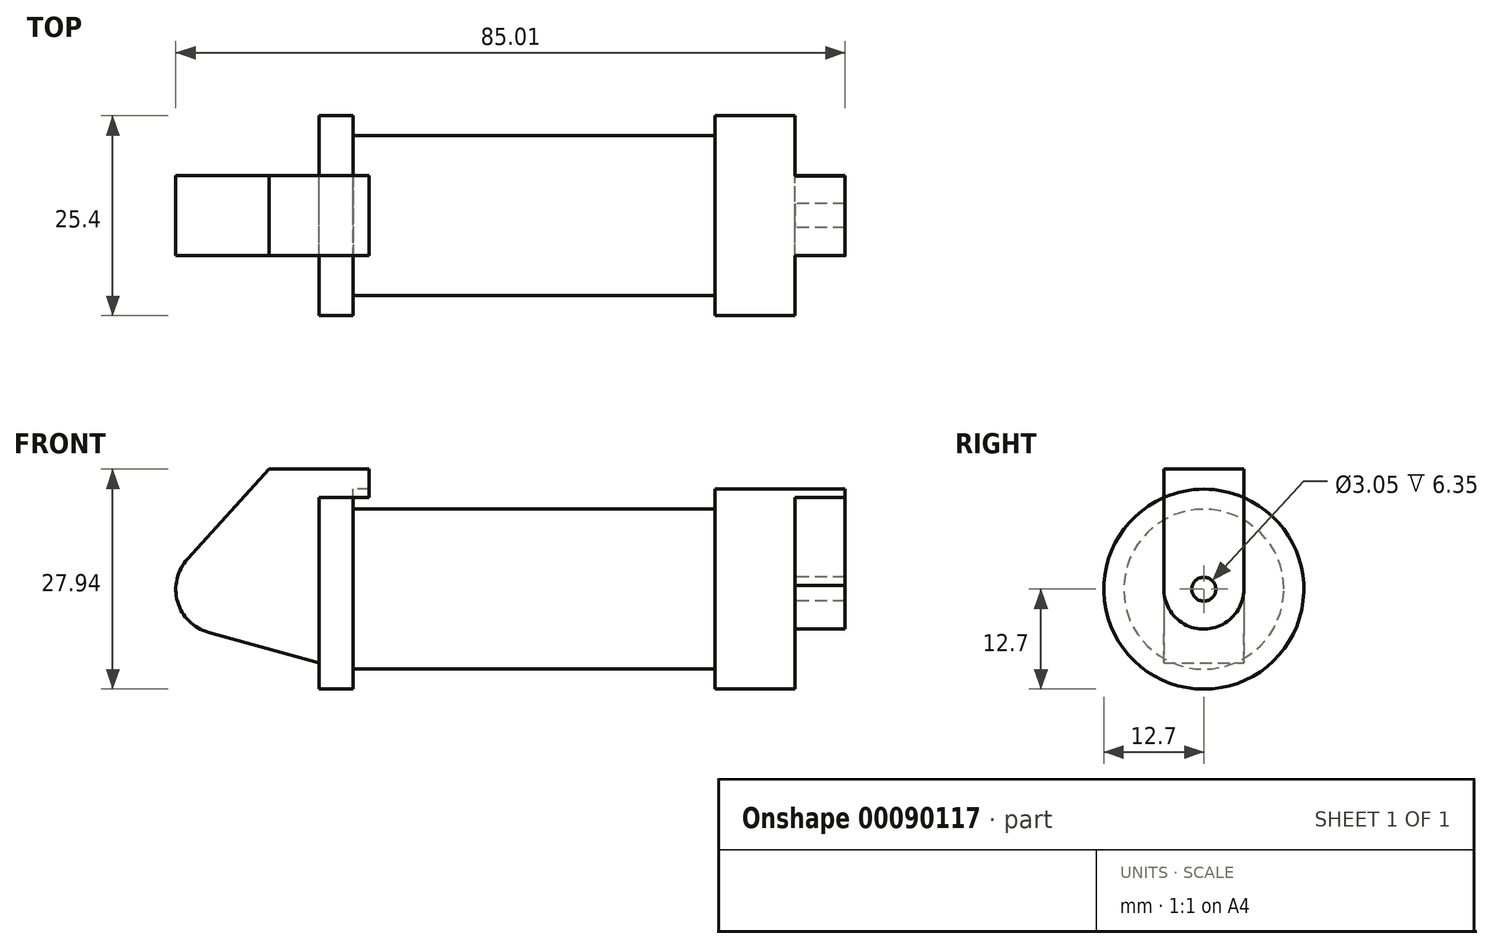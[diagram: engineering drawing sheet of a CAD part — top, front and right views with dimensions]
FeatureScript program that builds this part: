
annotation { "Feature Type Name" : "Feature", "Feature Type Description" : "" }
export const myFeature = defineFeature(function(context is Context, id is Id, definition is map)
    precondition{}
    {
        {
            var Q0;
            Q0=qCreatedBy(makeId("Front.planeOp"),FACE);
            var sketch = newSketch(context, id + "F0", { "sketchPlane" : qUnion([Q0])});
            skLineSegment(sketch, "E0", {"start": v(0, 0) * mm, "end": v(0, 12.7) * mm});
            skLineSegment(sketch, "E1", {"start": v(0, 12.7) * mm, "end": v(10.16, 12.7) * mm});
            skLineSegment(sketch, "E2", {"start": v(10.16, 12.7) * mm, "end": v(10.16, 10.16) * mm});
            skLineSegment(sketch, "E3", {"start": v(10.16, 10.16) * mm, "end": v(56.13, 10.16) * mm});
            skLineSegment(sketch, "E4", {"start": v(56.13, 10.16) * mm, "end": v(56.13, 12.7) * mm});
            skLineSegment(sketch, "E5", {"start": v(56.13, 12.7) * mm, "end": v(66.3, 12.7) * mm});
            skLineSegment(sketch, "E6", {"start": v(66.3, 12.7) * mm, "end": v(66.3, 0) * mm});
            skLineSegment(sketch, "E7", {"start": v(66.3, 0) * mm, "end": v(0, 0) * mm});
            skLineSegment(sketch, "E8", {"start": v(5.84, 15.24) * mm, "end": v(-0.5, 15.24) * mm});
            skLineSegment(sketch, "E9", {"start": v(-0.5, 15.24) * mm, "end": v(-10.88, 3.85) * mm});
            skLineSegment(sketch, "E10", {"start": v(0, 0) * mm, "end": v(-6.65, 0) * mm});
            skCircle(sketch, "E11", {"center": v(-6.65, 0) * mm, "radius": 5.72 * mm});
            skCircle(sketch, "E12", {"center": v(-6.65, 0) * mm, "radius": 3.18 * mm});
            skLineSegment(sketch, "E13", {"start": v(5.84, 15.24) * mm, "end": v(5.84, -9.4) * mm});
            skLineSegment(sketch, "E14", {"start": v(5.84, -9.4) * mm, "end": v(-8.18, -5.5) * mm});
            skSolve(sketch);
        }
        {
            var Q0;
            {var subQ0=sQuery(id+"F0.wireOp",EDGE,"E2");Q0=makeQuery(id+"F0.imprint","IMPRINT",FACE,{"disambiguationData":[TD([[makeQuery(id+"F0.imprint","IMPRINT",EDGE,{"derivedFrom":subQ0}),-1.0]])]});}
            var Q1;
            Q1=sQuery(id+"F0.wireOp",EDGE,"E7");
            revolve(context, id + "F1", {"entities" : qUnion([Q0]), "axis" : qUnion([Q1]), "revolveType" : RevolveType.FULL});
        }
        {
            var Q0;
            Q0=makeQuery(id+"FDnyFw9NJbFdQ6f_1.imprint","IMPRINT",FACE,{"disambiguationData":[TD([[makeQuery(id+"FDnyFw9NJbFdQ6f_1.imprint","IMPRINT",EDGE,{"derivedFrom":sQuery(id+"FDnyFw9NJbFdQ6f_1.wireOp",EDGE,"qFcc8gqR-njHb-6JYJ-WBu6-DDz6G6gH9gxF")}),1.0]])]});
            var sketch = newSketch(context, id + "F2", { "sketchPlane" : qUnion([Q0])});
            skCircle(sketch, "E15", {"center": v(-0.05, 0.02) * mm, "radius": 1.52 * mm});
            skCircle(sketch, "E16", {"center": v(-0.05, 0.02) * mm, "radius": 5.08 * mm});
            skSolve(sketch);
        }
        {
            var Q0;
            {var subQ0=sQuery(id+"F0.wireOp",EDGE,"E0");Q0=makeQuery(id+"F0.imprint","IMPRINT",FACE,{"disambiguationData":[TD([[makeQuery(id+"F0.imprint","IMPRINT",EDGE,{"derivedFrom":subQ0}),-1.0]])]});}
            var Q1;
            {var subQ3=sQuery(id+"F0.wireOp",EDGE,"E0");Q1=makeQuery(id+"F0.imprint","IMPRINT",FACE,{"disambiguationData":[TD([[makeQuery(id+"F0.imprint","IMPRINT",EDGE,{"derivedFrom":subQ3}),1.0]])]});}
            var Q2;
            {var subQ0=sQuery(id+"F0.wireOp",EDGE,"E12");Q2=makeQuery(id+"F0.imprint","IMPRINT",FACE,{"disambiguationData":[TD([[makeQuery(id+"F0.imprint","IMPRINT",EDGE,{"derivedFrom":subQ0}),1.0]])]});}
            var Q3;
            {var subQ4=sQuery(id+"F0.wireOp",EDGE,"E12");Q3=makeQuery(id+"F0.imprint","IMPRINT",FACE,{"disambiguationData":[TD([[makeQuery(id+"F0.imprint","IMPRINT",EDGE,{"derivedFrom":subQ4}),-1.0]])]});}
            var Q4;
            {var subQ0=sQuery(id+"F0.wireOp",EDGE,"E14");Q4=makeQuery(id+"F0.imprint","IMPRINT",FACE,{"disambiguationData":[TD([[makeQuery(id+"F0.imprint","IMPRINT",EDGE,{"derivedFrom":subQ0}),-1.0]])]});}
            extrude(context, id + "F3", {"entities" : qUnion([Q0, Q1, Q2, Q3, Q4]), "operationType" : NewBodyOperationType.ADD, "depth" : 5.08 * mm});
        }
        {
            var Q0;
            Q0 = qSketchRegion(id + "FazL3lt4DyqLLjs_1", true);
            var Q1;
            {var subQ0=sQuery(id+"F0.wireOp",EDGE,"E12");Q1=makeQuery(id+"F0.imprint","IMPRINT",FACE,{"disambiguationData":[TD([[makeQuery(id+"F0.imprint","IMPRINT",EDGE,{"derivedFrom":subQ0}),1.0]])]});}
            var Q2;
            {var subQ3=sQuery(id+"F0.wireOp",EDGE,"E0");Q2=makeQuery(id+"F0.imprint","IMPRINT",FACE,{"disambiguationData":[TD([[makeQuery(id+"F0.imprint","IMPRINT",EDGE,{"derivedFrom":subQ3}),1.0]])]});}
            var Q3;
            {var subQ0=sQuery(id+"F0.wireOp",EDGE,"E14");Q3=makeQuery(id+"F0.imprint","IMPRINT",FACE,{"disambiguationData":[TD([[makeQuery(id+"F0.imprint","IMPRINT",EDGE,{"derivedFrom":subQ0}),-1.0]])]});}
            var Q4;
            {var subQ4=sQuery(id+"F0.wireOp",EDGE,"E12");Q4=makeQuery(id+"F0.imprint","IMPRINT",FACE,{"disambiguationData":[TD([[makeQuery(id+"F0.imprint","IMPRINT",EDGE,{"derivedFrom":subQ4}),-1.0]])]});}
            var Q5;
            {var subQ0=sQuery(id+"F0.wireOp",EDGE,"E0");Q5=makeQuery(id+"F0.imprint","IMPRINT",FACE,{"disambiguationData":[TD([[makeQuery(id+"F0.imprint","IMPRINT",EDGE,{"derivedFrom":subQ0}),-1.0]])]});}
            var Q6;
            Q6 = qSketchRegion(id + "F2", true);
            extrude(context, id + "F4", {"entities" : qUnion([Q0, Q1, Q2, Q3, Q4, Q5, Q6]), "operationType" : NewBodyOperationType.ADD, "oppositeDirection" : true, "depth" : 5.08 * mm});
        }
        {
            var Q0;
            Q0=makeQuery(id+"F1.opRevolve","SWEPT_FACE",FACE,{"disambiguationData":[OSD([sQuery(id+"F0.wireOp",EDGE,"E6")])]});
            var sketch = newSketch(context, id + "F5", { "sketchPlane" : qUnion([Q0])});
            skCircle(sketch, "E17", {"center": v(0, 0) * mm, "radius": 1.52 * mm});
            skCircle(sketch, "E18", {"center": v(0, 0) * mm, "radius": 5.08 * mm});
            skLineSegment(sketch, "E19", {"start": v(5.06, 15.2) * mm, "end": v(5.08, 0) * mm});
            skLineSegment(sketch, "E20", {"start": v(-5.06, 15.24) * mm, "end": v(-5.06, 0) * mm});
            skSolve(sketch);
        }
        {
            var Q0;
            Q0=makeQuery(id+"F5.imprint","IMPRINT",FACE,{"disambiguationData":[TD([[makeQuery(id+"F5.imprint","IMPRINT",EDGE,{"derivedFrom":sQuery(id+"F5.wireOp",EDGE,"E17")}),-1.0]])]});
            var Q1;
            {var subQ0=sQuery(id+"F5.wireOp",EDGE,"E19");var subQ1=sQuery(id+"F5.wireOp",EDGE,"E18");var subQ2=makeQuery(id+"F5.imprint","INTERSECT",VERTEX,{"derivedFrom":[subQ1,subQ0]});Q1=makeQuery(id+"F5.imprint","IMPRINT",FACE,{"disambiguationData":[TD([[makeQuery(id+"F5.imprint","IMPRINT",EDGE,{"disambiguationData":[TD([[subQ2,-1.0]])],"derivedFrom":subQ1}),-1.0]])]});}
            var Q2;
            {var subQ0=sQuery(id+"F0.wireOp",EDGE,"E13");Q2=makeQuery(id+"F4.boolean.opBoolean","MERGE",FACE,{"derivedFrom":[makeQuery(id+"F3.opExtrude","SWEPT_FACE",FACE,{"disambiguationData":[OSD([subQ0])]}),makeQuery(id+"F4.opExtrude","SWEPT_FACE",FACE,{"disambiguationData":[OSD([subQ0])]})]});}
            extrude(context, id + "F6", {"entities" : qUnion([Q0, Q1, Q2]), "operationType" : NewBodyOperationType.ADD, "depth" : 6.35 * mm});
        }
    });
